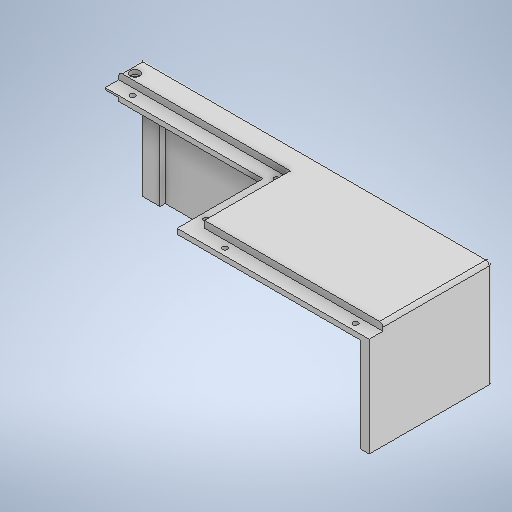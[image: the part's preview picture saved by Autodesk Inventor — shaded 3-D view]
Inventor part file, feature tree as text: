
AUTODESK INVENTOR PART (.ipt)
format: ipt  version: 2025.2 (Build 292293000, 293)  size: 761,344 bytes
history: native  units: mm
features: extrude x12, sketch x12, other x1, fillet x1
ambient origin geometry x8: Origin, YZ Plane, XZ Plane, XY Plane, X Axis, Y Axis, Z Axis, Center Point
bodies: Body1 (feature_tree)
feature tree (26):
  other  "ソリッド1"
  extrude  "押し出し1"  Depth=204.0mm
  extrude  "押し出し2"  Depth=72.0mm
  extrude  "押し出し3"  Depth=7.0mm TaperAngle=0.0deg
  extrude  "押し出し4"  Depth=92.0mm
  extrude  "押し出し5"  Depth=50.0mm
  extrude  "押し出し6"  TaperAngle=0.0deg  [1 undecoded]
  extrude  "押し出し7"  Depth=8.0mm
  extrude  "押し出し8"  Depth=4.0mm TaperAngle=0.0deg
  extrude  "押し出し9"  Depth=8.0mm
  extrude  "押し出し10"  Depth=8.0mm
  extrude  "押し出し11"  Depth=3.0mm
  extrude  "押し出し12"  Depth=3.0mm
  fillet  "フィレット1"  Radius=3.0mm
  sketch  "スケッチ1"
  sketch  "スケッチ2"
  sketch  "スケッチ3"
  sketch  "スケッチ4"
  sketch  "スケッチ5"
  sketch  "スケッチ6"
  sketch  "スケッチ7"
  sketch  "スケッチ8"
  sketch  "スケッチ9"
  sketch  "スケッチ10"
  sketch  "スケッチ11"
  sketch  "スケッチ12"
note: 1 required parameter value undecoded (feature->parameter linkage not recoverable at this tier; creation-order binding heuristic only, values carry confidence <= 0.55)
